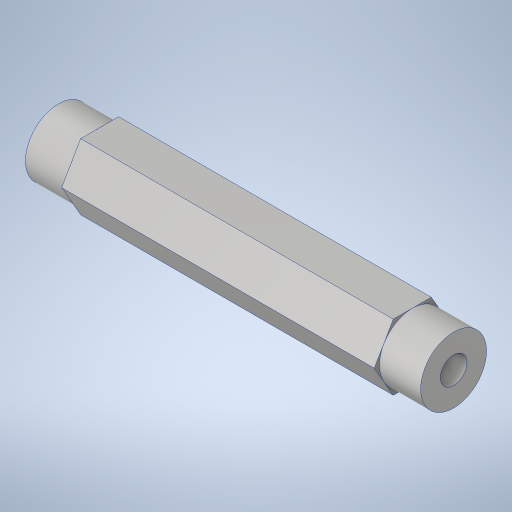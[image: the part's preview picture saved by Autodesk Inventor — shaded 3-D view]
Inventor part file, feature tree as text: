
AUTODESK INVENTOR PART (.ipt)
format: ipt  version: 2023.4 (Build 274418000, 418)  size: 255,488 bytes
history: native  units: in
note: dims shown in document units (in); Inventor stores cm internally (conversion verified against a paired STEP export)
features: sketch x4, extrude x3, hole x1, projected_geometry x1
ambient origin geometry x8: Origin, YZ Plane, XZ Plane, XY Plane, X Axis, Y Axis, Z Axis, Center Point
bodies: Solid1 (feature_tree)
feature tree (9):
  extrude  "Extrusion1"  Depth=2.374in TaperAngle=0.0deg
  extrude  "Extrusion2"  Depth=0.313in TaperAngle=0.0deg
  extrude  "Extrusion3"  Depth=0.313in TaperAngle=0.0deg
  hole  "Hole1"  [1 undecoded]
  sketch  "Sketch1"  dims[d0=0.5in d1=2.374in d2=0.0in]
  sketch  "Sketch2"  dims[d3=0.5in d4=0.313in d5=0.0in]
  sketch  "Sketch3"  dims[d6=0.5in d7=0.313in d8=0.0in]
  sketch  "Sketch4"  dims[d9=0.201in d10=0.75in d11=0.385in d12=0.25in d13=0.5635in d14=1.0in d15=0.8108in]
  projected_geometry  "Projected Loop1"
note: 1 required parameter value undecoded (feature->parameter linkage not recoverable at this tier; creation-order binding heuristic only, values carry confidence <= 0.55)
